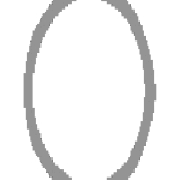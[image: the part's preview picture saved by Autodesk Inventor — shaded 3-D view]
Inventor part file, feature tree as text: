
AUTODESK INVENTOR PART (.ipt)
format: ipt  version: 2021 (Build 250183000, 183)  size: 112,640 bytes
history: native  units: in
note: dims shown in document units (in); Inventor stores cm internally (conversion verified against a paired STEP export)
features: other x4, sketch x3, plane x1
ambient origin geometry x8: Origin, YZ Plane, XZ Plane, XY Plane, X Axis, Y Axis, Z Axis, Center Point
bodies: Solid1 (feature_tree), Body (feature_tree)
feature tree (8):
  other  "Driven Length"
  other  "Frame Generator"
  other  "Start Plane"
  other  "End Plane"
  sketch  "Sketch"  dims[d2=13.0in d4=-0.0in d5=13.0in d6=0.12in d7=0.0in d8=90.0deg d9=13.0in]
  sketch  "Sketch2"  dims[d0=1.0in]
  plane  "Work Plane3"
  sketch  "Sketch3"  dims[d1=0.065in]
